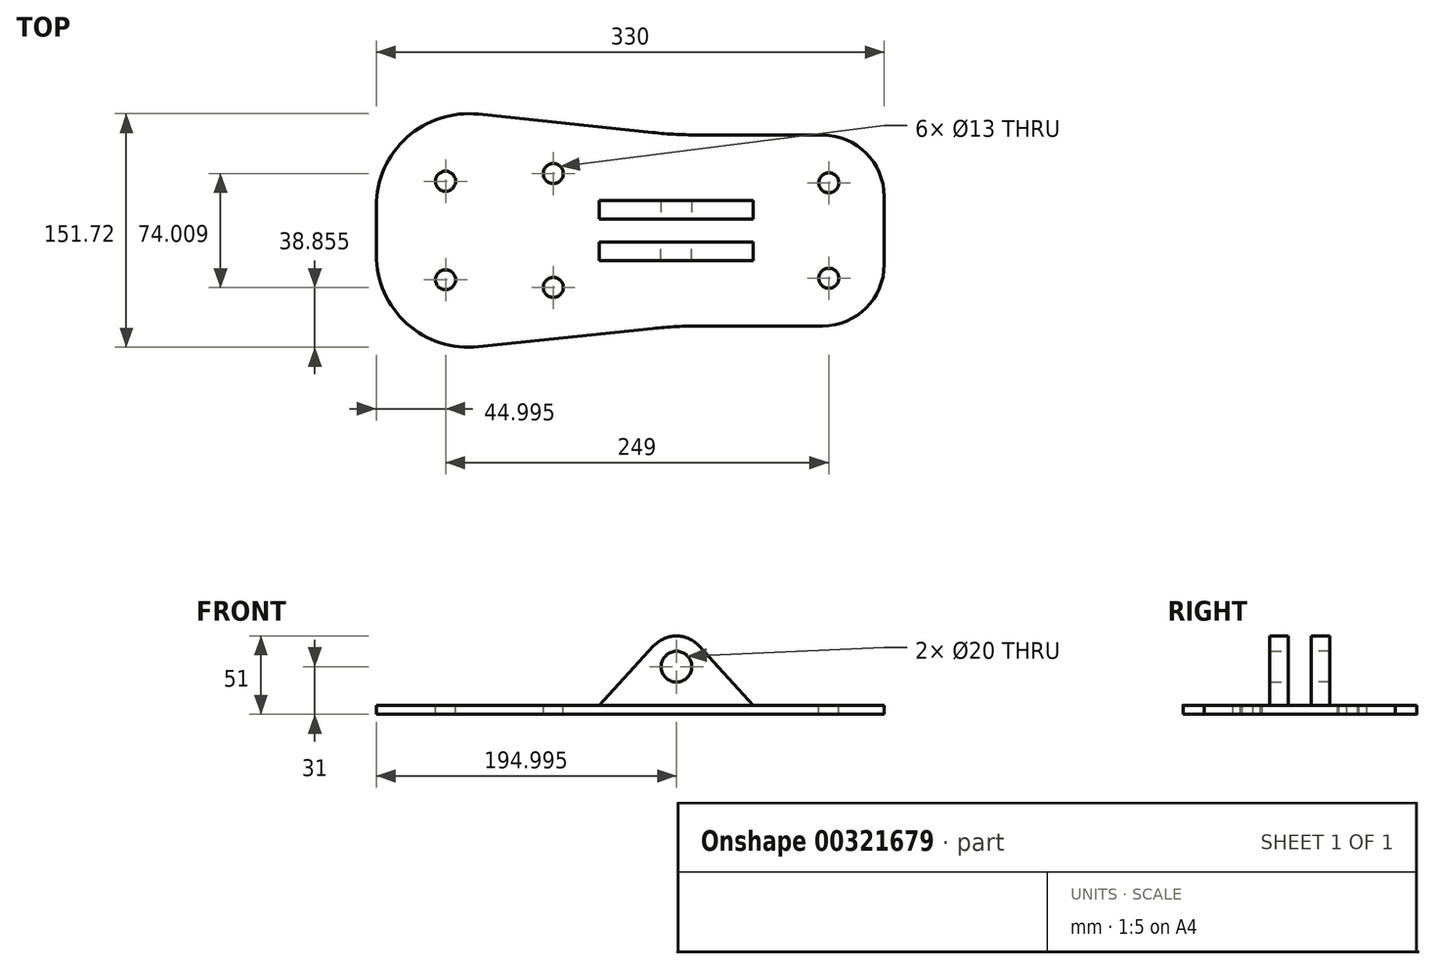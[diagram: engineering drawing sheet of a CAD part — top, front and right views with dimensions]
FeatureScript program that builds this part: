
annotation { "Feature Type Name" : "Feature", "Feature Type Description" : "" }
export const myFeature = defineFeature(function(context is Context, id is Id, definition is map)
    precondition{}
    {
        {
            var Q0;
            Q0=qCreatedBy(makeId("Top.planeOp"),FACE);
            var sketch = newSketch(context, id + "F0", { "sketchPlane" : qUnion([Q0])});
            skLineSegment(sketch, "E0", {"start": v(-93.13, 82.5) * mm, "end": v(-93.13, -82.5) * mm});
            skLineSegment(sketch, "E1", {"start": v(-93.13, 82.5) * mm, "end": v(101.87, 62) * mm});
            skLineSegment(sketch, "E2", {"start": v(101.87, 62) * mm, "end": v(236.87, 62) * mm});
            skLineSegment(sketch, "E3", {"start": v(236.87, 62) * mm, "end": v(236.87, -62) * mm});
            skLineSegment(sketch, "E4", {"start": v(236.87, -62) * mm, "end": v(101.87, -62) * mm});
            skLineSegment(sketch, "E5", {"start": v(101.87, -62) * mm, "end": v(-93.13, -82.5) * mm});
            skSolve(sketch);
        }
        {
            var Q0;
            Q0=makeQuery(id+"F0.imprint","IMPRINT",FACE,{"disambiguationData":[TD([[makeQuery(id+"F0.imprint","IMPRINT",EDGE,{"derivedFrom":sQuery(id+"F0.wireOp",EDGE,"E0")}),1.0]])]});
            extrude(context, id + "F1", {"entities" : qUnion([Q0]), "depth" : 6 * mm});
        }
        {
            var Q0;
            Q0=makeQuery(id+"F1.opExtrude","SWEPT_EDGE",EDGE,{"disambiguationData":[OSD([sQuery(id+"F0.wireOp",EDGE,"E0"),sQuery(id+"F0.wireOp",EDGE,"E5")])]});
            var Q1;
            Q1=makeQuery(id+"F1.opExtrude","SWEPT_EDGE",EDGE,{"disambiguationData":[OSD([sQuery(id+"F0.wireOp",EDGE,"E0"),sQuery(id+"F0.wireOp",EDGE,"E1")])]});
            fillet(context, id + "F2", {"entities" : qUnion([Q0, Q1]), "radius" : 60 * mm, "tangentPropagation" : true, "allowEdgeOverflow" : false});
        }
        {
            var Q0;
            Q0=makeQuery(id+"F1.opExtrude","SWEPT_EDGE",EDGE,{"disambiguationData":[OSD([sQuery(id+"F0.wireOp",EDGE,"E3"),sQuery(id+"F0.wireOp",EDGE,"E4")])]});
            var Q1;
            Q1=makeQuery(id+"F1.opExtrude","SWEPT_EDGE",EDGE,{"disambiguationData":[OSD([sQuery(id+"F0.wireOp",EDGE,"E2"),sQuery(id+"F0.wireOp",EDGE,"E3")])]});
            fillet(context, id + "F3", {"entities" : qUnion([Q0, Q1]), "radius" : 40 * mm, "tangentPropagation" : true, "allowEdgeOverflow" : false});
        }
        {
            var Q0;
            Q0=makeQuery(id+"F1.opExtrude","SWEPT_EDGE",EDGE,{"disambiguationData":[OSD([sQuery(id+"F0.wireOp",EDGE,"E4"),sQuery(id+"F0.wireOp",EDGE,"E5")])]});
            var Q1;
            Q1=makeQuery(id+"F1.opExtrude","SWEPT_EDGE",EDGE,{"disambiguationData":[OSD([sQuery(id+"F0.wireOp",EDGE,"E1"),sQuery(id+"F0.wireOp",EDGE,"E2")])]});
            fillet(context, id + "F4", {"entities" : qUnion([Q0, Q1]), "radius" : 300 * mm, "tangentPropagation" : true, "allowEdgeOverflow" : false});
        }
        {
            var Q0;
            Q0=qCreatedBy(makeId("Front.planeOp"),FACE);
            var sketch = newSketch(context, id + "F5", { "sketchPlane" : qUnion([Q0])});
            skArc(sketch, "E6", {"start": v(116.62, 44.5) * mm, "mid": v(101.87, 51) * mm, "end": v(87.11, 44.5) * mm});
            skLineSegment(sketch, "E7", {"start": v(101.87, 31) * mm, "end": v(101.87, -10.9) * mm, "construction": true});
            skLineSegment(sketch, "E8.0", {"start": v(51.87, 31) * mm, "end": v(51.87, 6) * mm, "construction": true});
            skLineSegment(sketch, "E9.0", {"start": v(151.87, 31) * mm, "end": v(151.87, 6) * mm, "construction": true});
            skLineSegment(sketch, "E10.0", {"start": v(151.87, 6) * mm, "end": v(86.23, 6) * mm});
            skPoint(sketch, "E11.orphan", {"position": v(86.23, 6) * mm});
            skPoint(sketch, "E12.orphan", {"position": v(-26.86, 6) * mm});
            skLineSegment(sketch, "E13", {"start": v(151.87, 6) * mm, "end": v(116.62, 44.5) * mm});
            skLineSegment(sketch, "E14.0", {"start": v(86.23, 6) * mm, "end": v(51.87, 6) * mm});
            skLineSegment(sketch, "E15", {"start": v(51.87, 6) * mm, "end": v(87.11, 44.5) * mm});
            skCircle(sketch, "E16", {"center": v(101.87, 31) * mm, "radius": 10 * mm});
            skSolve(sketch);
        }
        {
            var Q0;
            Q0=qCreatedBy(makeId("Front.planeOp"),FACE);
            cPlane(context, id + "F6", {"entities" : qUnion([Q0]), "cplaneType" : CPlaneType.OFFSET, "offset" : 7.5 * mm, "width" : 150 * mm, "height" : 150 * mm});
        }
        {
            var Q0;
            Q0=qCreatedBy(makeId("Front.planeOp"),FACE);
            cPlane(context, id + "F7", {"entities" : qUnion([Q0]), "cplaneType" : CPlaneType.OFFSET, "offset" : 7.5 * mm, "oppositeDirection" : true, "width" : 150 * mm, "height" : 150 * mm});
        }
        {
            var Q0;
            Q0=qCreatedBy(id+"F7.planeOp",FACE);
            var sketch = newSketch(context, id + "F8", { "sketchPlane" : qUnion([Q0])});
            skArc(sketch, "E17.0", {"start": v(116.62, 44.5) * mm, "mid": v(101.87, 51) * mm, "end": v(87.11, 44.5) * mm});
            skLineSegment(sketch, "E17.1", {"start": v(101.87, 31) * mm, "end": v(101.87, -10.9) * mm, "construction": true});
            skLineSegment(sketch, "E17.2", {"start": v(51.87, 31) * mm, "end": v(51.87, 6) * mm, "construction": true});
            skLineSegment(sketch, "E17.3", {"start": v(151.87, 31) * mm, "end": v(151.87, 6) * mm, "construction": true});
            skLineSegment(sketch, "E17.4", {"start": v(151.87, 6) * mm, "end": v(86.23, 6) * mm});
            skPoint(sketch, "E17.5", {"position": v(86.23, 6) * mm});
            skPoint(sketch, "E17.6", {"position": v(-26.86, 6) * mm});
            skLineSegment(sketch, "E17.7", {"start": v(151.87, 6) * mm, "end": v(116.62, 44.5) * mm});
            skLineSegment(sketch, "E17.8", {"start": v(86.23, 6) * mm, "end": v(51.87, 6) * mm});
            skLineSegment(sketch, "E17.9", {"start": v(51.87, 6) * mm, "end": v(87.11, 44.5) * mm});
            skCircle(sketch, "E17.10", {"center": v(101.87, 31) * mm, "radius": 10 * mm});
            skSolve(sketch);
        }
        {
            var Q0;
            Q0=qCreatedBy(id+"F6.planeOp",FACE);
            var sketch = newSketch(context, id + "F9", { "sketchPlane" : qUnion([Q0])});
            skArc(sketch, "E18.0", {"start": v(116.62, 44.5) * mm, "mid": v(101.87, 51) * mm, "end": v(87.11, 44.5) * mm});
            skLineSegment(sketch, "E18.1", {"start": v(101.87, 31) * mm, "end": v(101.87, -10.9) * mm, "construction": true});
            skLineSegment(sketch, "E18.2", {"start": v(51.87, 31) * mm, "end": v(51.87, 6) * mm, "construction": true});
            skLineSegment(sketch, "E18.3", {"start": v(151.87, 31) * mm, "end": v(151.87, 6) * mm, "construction": true});
            skLineSegment(sketch, "E18.4", {"start": v(151.87, 6) * mm, "end": v(86.23, 6) * mm});
            skPoint(sketch, "E18.5", {"position": v(86.23, 6) * mm});
            skPoint(sketch, "E18.6", {"position": v(-26.86, 6) * mm});
            skLineSegment(sketch, "E18.7", {"start": v(151.87, 6) * mm, "end": v(116.62, 44.5) * mm});
            skLineSegment(sketch, "E18.8", {"start": v(86.23, 6) * mm, "end": v(51.87, 6) * mm});
            skLineSegment(sketch, "E18.9", {"start": v(51.87, 6) * mm, "end": v(87.11, 44.5) * mm});
            skCircle(sketch, "E18.10", {"center": v(101.87, 31) * mm, "radius": 10 * mm});
            skSolve(sketch);
        }
        {
            var Q0;
            Q0 = qSketchRegion(id + "F8", true);
            extrude(context, id + "F10", {"entities" : qUnion([Q0]), "operationType" : NewBodyOperationType.ADD, "oppositeDirection" : true, "depth" : 12 * mm});
        }
        {
            var Q0;
            Q0 = qSketchRegion(id + "F9", true);
            extrude(context, id + "F11", {"entities" : qUnion([Q0]), "operationType" : NewBodyOperationType.ADD, "depth" : 12 * mm});
        }
        {
            var Q0;
            Q0=makeQuery(id+"F1.opExtrude","CAP_FACE",FACE,{"disambiguationData":[OSD([sQuery(id+"F0.wireOp",EDGE,"E0"),sQuery(id+"F0.wireOp",EDGE,"E1"),sQuery(id+"F0.wireOp",EDGE,"E2"),sQuery(id+"F0.wireOp",EDGE,"E3"),sQuery(id+"F0.wireOp",EDGE,"E4"),sQuery(id+"F0.wireOp",EDGE,"E5")])],"isStart":false});
            var sketch = newSketch(context, id + "F12", { "sketchPlane" : qUnion([Q0])});
            skCircle(sketch, "E19", {"center": v(200.87, 31) * mm, "radius": 6.5 * mm});
            skCircle(sketch, "E20", {"center": v(200.87, -31) * mm, "radius": 6.5 * mm});
            skCircle(sketch, "E21", {"center": v(21.87, 37) * mm, "radius": 6.5 * mm});
            skCircle(sketch, "E22", {"center": v(-48.13, 32) * mm, "radius": 6.5 * mm});
            skCircle(sketch, "E23", {"center": v(-48.13, -32) * mm, "radius": 6.5 * mm});
            skCircle(sketch, "E24", {"center": v(21.87, -37) * mm, "radius": 6.5 * mm});
            skSolve(sketch);
        }
        {
            var Q0;
            Q0 = qSketchRegion(id + "F12", true);
            extrude(context, id + "F13", {"entities" : qUnion([Q0]), "operationType" : NewBodyOperationType.REMOVE, "oppositeDirection" : true, "depth" : 25 * mm});
        }
    });
